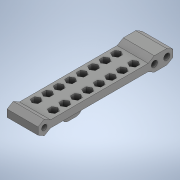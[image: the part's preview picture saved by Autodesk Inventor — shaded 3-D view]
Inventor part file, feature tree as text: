
AUTODESK INVENTOR PART (.ipt)
format: ipt  version: 2020 (Build 240168000, 168)  size: 480,768 bytes
history: native  units: in
note: dims shown in document units (in); Inventor stores cm internally (conversion verified against a paired STEP export)
features: sketch x7, extrude x6, projected_geometry x4, plane x2, mirror x1, fillet x1
ambient origin geometry x8: Origin, YZ Plane, XZ Plane, XY Plane, X Axis, Y Axis, Z Axis, Center Point
bodies: Solid1 (feature_tree)
feature tree (21):
  extrude  "Extrusion1"  Depth=3.4256in
  plane  "Work Plane1"
  extrude  "Extrusion2"  Depth=0.7874in
  sketch  "Sketch4"  dims[d4=0.0in d5=0.0827in]
  extrude  "Extrusion4"  Depth=0.0827in
  plane  "Work Plane2"
  extrude  "Extrusion6"  Depth=3.1106in
  mirror  "Mirror2"
  extrude  "Extrusion7"  Depth=0.315in
  extrude  "Extrusion8"  Depth=0.2362in
  fillet  "Fillet1"  [1 undecoded]
  sketch  "Sketch1"  dims[d0=0.1818in d1=3.4256in]
  sketch  "Sketch2"  dims[d2=0.1378in d3=0.7874in]
  sketch  "Sketch5"  dims[d6=0.7874in d7=0.0in d28=3.1106in]
  sketch  "Sketch7"  dims[d29=0.315in d31=0.315in]
  projected_geometry  "Projected Loop7"
  projected_geometry  "Projected Loop8"
  sketch  "Sketch8"  dims[d33=0.1575in d34=0.2362in d35=0.0in]
  projected_geometry  "Projected Loop9"
  sketch  "Sketch10"  dims[d38=0.315in d39=0.2756in d40=-0.3092in d41=0.0787in d42=0.0787in d43=0.0787in d44=3.1496in d46=0.2913in d47=0.3937in d49=0.3937in d51=3.1496in d53=0.2913in d54=0.3937in d56=0.3937in d58=0.0in d59=0.0in d60=1.0994in d61=0.1378in d63=1.1811in d64=0.1575in d65=0.0in d66=0.126in d67=0.1575in]
  projected_geometry  "Projected Loop10"
note: 1 required parameter value undecoded (feature->parameter linkage not recoverable at this tier; creation-order binding heuristic only, values carry confidence <= 0.55)
